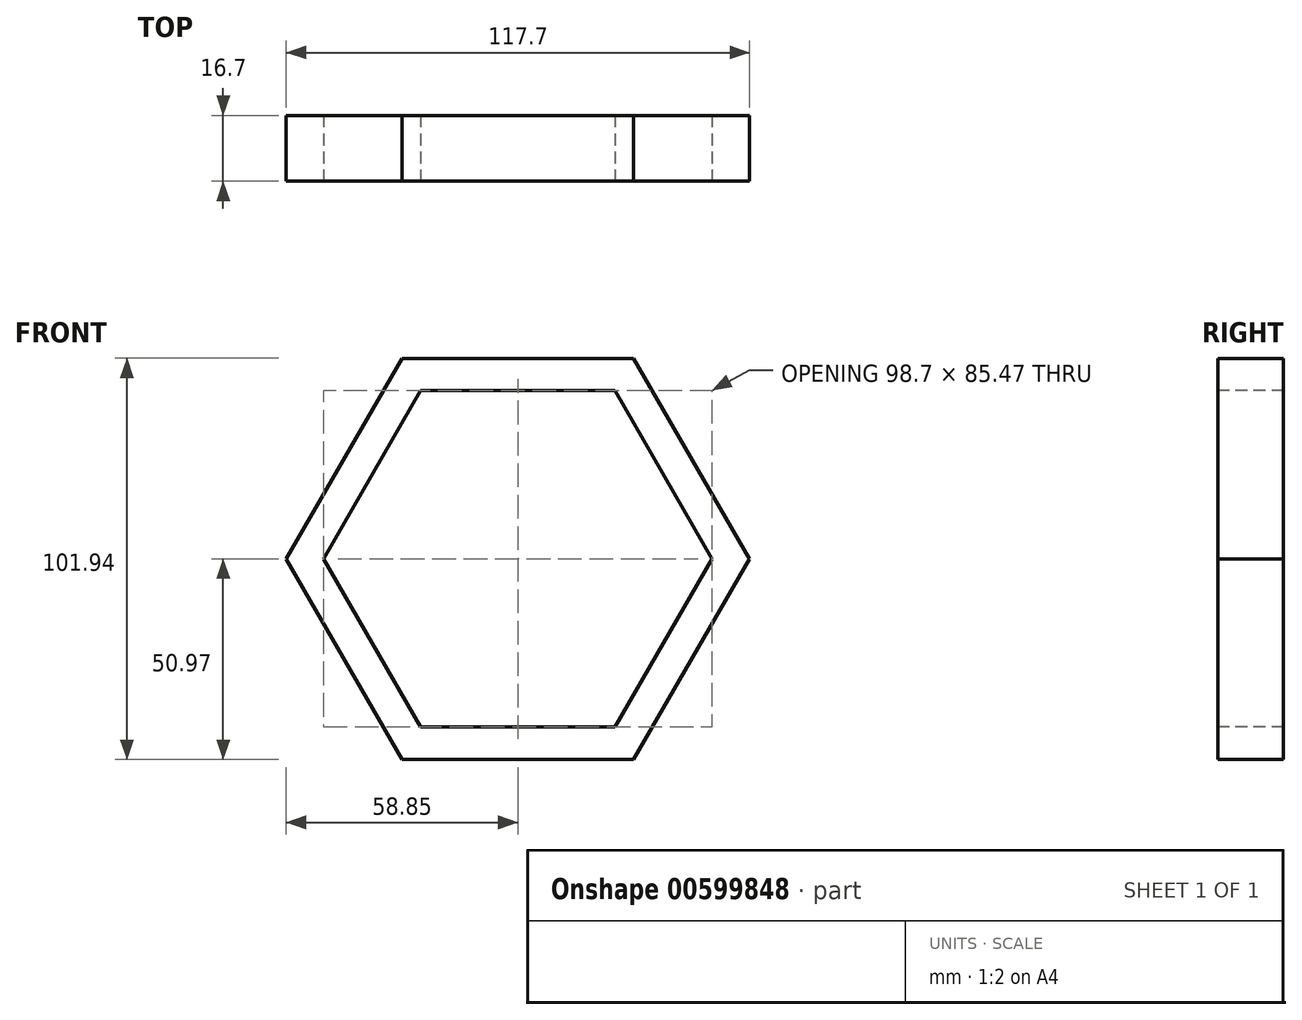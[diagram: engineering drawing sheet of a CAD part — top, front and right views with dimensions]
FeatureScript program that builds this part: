
annotation { "Feature Type Name" : "Feature", "Feature Type Description" : "" }
export const myFeature = defineFeature(function(context is Context, id is Id, definition is map)
    precondition{}
    {
        {
            var Q0;
            Q0=qCreatedBy(makeId("Front.planeOp"),FACE);
            var sketch = newSketch(context, id + "F0", { "sketchPlane" : qUnion([Q0])});
            skCircle(sketch, "E0.cCircle", {"center": v(0, 0) * mm, "radius": 50.97 * mm, "construction": true});
            skLineSegment(sketch, "E0.0", {"start": v(-29.43, 50.97) * mm, "end": v(29.43, 50.97) * mm});
            skLineSegment(sketch, "E0.1", {"start": v(29.43, 50.97) * mm, "end": v(58.85, 0) * mm});
            skLineSegment(sketch, "E0.2", {"start": v(58.85, 0) * mm, "end": v(29.43, -50.97) * mm});
            skLineSegment(sketch, "E0.3", {"start": v(29.43, -50.97) * mm, "end": v(-29.43, -50.97) * mm});
            skLineSegment(sketch, "E0.4", {"start": v(-29.43, -50.97) * mm, "end": v(-58.85, 0) * mm});
            skLineSegment(sketch, "E0.5", {"start": v(-58.85, 0) * mm, "end": v(-29.43, 50.97) * mm});
            skPoint(sketch, "E0.0.midPoint", {"position": v(0, 50.97) * mm});
            skSolve(sketch);
        }
        {
            var Q0;
            Q0=makeQuery(id+"F0.imprint","IMPRINT",FACE,{"disambiguationData":[TD([[makeQuery(id+"F0.imprint","IMPRINT",EDGE,{"derivedFrom":sQuery(id+"F0.wireOp",EDGE,"E0.0")}),-1.0]])]});
            var sketch = newSketch(context, id + "F1", { "sketchPlane" : qUnion([Q0])});
            skLineSegment(sketch, "E1", {"start": v(0, 50.45) * mm, "end": v(0, -49.03) * mm});
            skSolve(sketch);
        }
        {
            var Q0;
            Q0=makeQuery(id+"F1.imprint","IMPRINT",FACE,{"disambiguationData":[TD([[makeQuery(id+"F1.imprint","IMPRINT",EDGE,{"derivedFrom":makeQuery(id+"F0.imprint","IMPRINT",EDGE,{"derivedFrom":sQuery(id+"F0.wireOp",EDGE,"E0.0")})}),-1.0]])]});
            extrude(context, id + "F2", {"entities" : qUnion([Q0]), "depth" : 16.7 * mm, "offsetDistance" : 25 * mm});
        }
        {
            var Q0;
            Q0=makeQuery(id+"F2.opExtrude","CAP_FACE",FACE,{"disambiguationData":[OSD([sQuery(id+"F0.wireOp",EDGE,"E0.0"),sQuery(id+"F0.wireOp",EDGE,"E0.1"),sQuery(id+"F0.wireOp",EDGE,"E0.2"),sQuery(id+"F0.wireOp",EDGE,"E0.3"),sQuery(id+"F0.wireOp",EDGE,"E0.4"),sQuery(id+"F0.wireOp",EDGE,"E0.5")])],"isStart":false});
            var sketch = newSketch(context, id + "F3", { "sketchPlane" : qUnion([Q0])});
            skCircle(sketch, "E2.cCircle", {"center": v(0, 0) * mm, "radius": 42.74 * mm, "construction": true});
            skLineSegment(sketch, "E2.0", {"start": v(-24.67, 42.74) * mm, "end": v(24.67, 42.74) * mm});
            skLineSegment(sketch, "E2.1", {"start": v(24.67, 42.74) * mm, "end": v(49.35, 0) * mm});
            skLineSegment(sketch, "E2.2", {"start": v(49.35, 0) * mm, "end": v(24.67, -42.74) * mm});
            skLineSegment(sketch, "E2.3", {"start": v(24.67, -42.74) * mm, "end": v(-24.67, -42.74) * mm});
            skLineSegment(sketch, "E2.4", {"start": v(-24.67, -42.74) * mm, "end": v(-49.35, 0) * mm});
            skLineSegment(sketch, "E2.5", {"start": v(-49.35, 0) * mm, "end": v(-24.67, 42.74) * mm});
            skPoint(sketch, "E2.0.midPoint", {"position": v(0, 42.74) * mm});
            skSolve(sketch);
        }
        {
            var Q0;
            Q0=makeQuery(id+"F3.imprint","IMPRINT",FACE,{"disambiguationData":[TD([[makeQuery(id+"F3.imprint","IMPRINT",EDGE,{"derivedFrom":sQuery(id+"F3.wireOp",EDGE,"E2.0")}),-1.0]])]});
            extrude(context, id + "F4", {"entities" : qUnion([Q0]), "operationType" : NewBodyOperationType.REMOVE, "oppositeDirection" : true, "depth" : 47.6 * mm, "offsetDistance" : 25 * mm});
        }
    });
